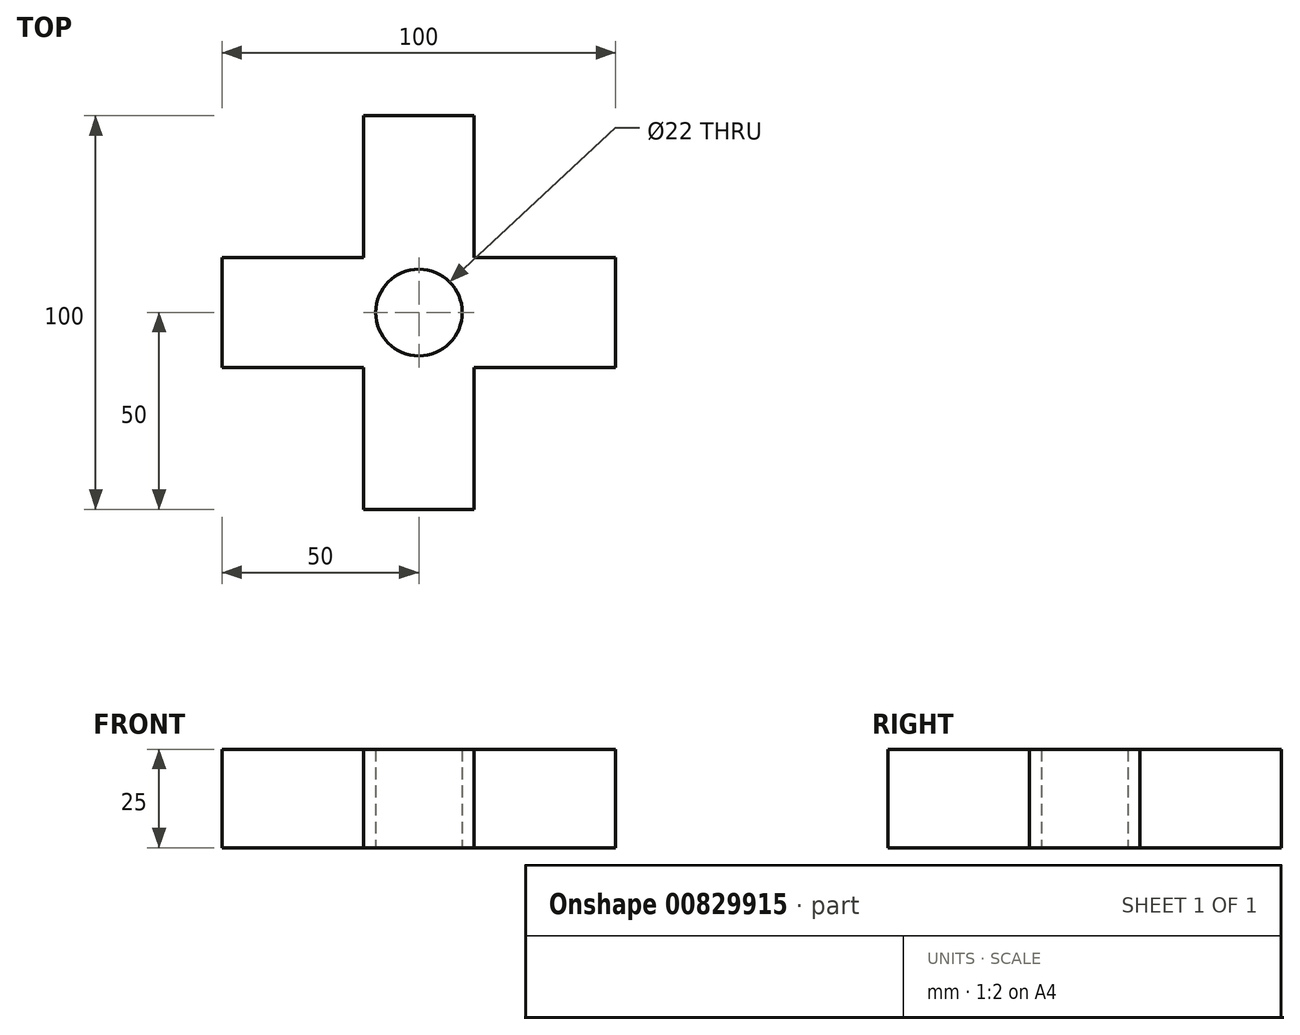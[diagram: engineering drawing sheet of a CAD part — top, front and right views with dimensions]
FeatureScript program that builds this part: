
annotation { "Feature Type Name" : "Feature", "Feature Type Description" : "" }
export const myFeature = defineFeature(function(context is Context, id is Id, definition is map)
    precondition{}
    {
        {
            var Q0;
            Q0=qCreatedBy(makeId("Top.planeOp"),FACE);
            var sketch = newSketch(context, id + "F0", { "sketchPlane" : qUnion([Q0])});
            skCircle(sketch, "E0", {"center": v(0, 0) * mm, "radius": 11 * mm});
            skPoint(sketch, "E1.oppositeSnap0", {"position": v(14, 7) * mm});
            skLineSegment(sketch, "E2.top", {"start": v(-14, 50) * mm, "end": v(14, 50) * mm});
            skLineSegment(sketch, "E2.left", {"start": v(-14, 14) * mm, "end": v(-14, 50) * mm});
            skLineSegment(sketch, "E2.right", {"start": v(14, 14) * mm, "end": v(14, 50) * mm});
            skLineSegment(sketch, "E3.bottom", {"start": v(14, 14) * mm, "end": v(50, 14) * mm});
            skLineSegment(sketch, "E3.top", {"start": v(14, -14) * mm, "end": v(50, -14) * mm});
            skLineSegment(sketch, "E3.right", {"start": v(50, 14) * mm, "end": v(50, -14) * mm});
            skLineSegment(sketch, "E4.top", {"start": v(-14, -50) * mm, "end": v(14, -50) * mm});
            skLineSegment(sketch, "E4.left", {"start": v(-14, -14) * mm, "end": v(-14, -50) * mm});
            skLineSegment(sketch, "E4.right", {"start": v(14, -14) * mm, "end": v(14, -50) * mm});
            skLineSegment(sketch, "E5.bottom", {"start": v(-14, 14) * mm, "end": v(-50, 14) * mm});
            skLineSegment(sketch, "E5.top", {"start": v(-14, -14) * mm, "end": v(-50, -14) * mm});
            skLineSegment(sketch, "E5.right", {"start": v(-50, 14) * mm, "end": v(-50, -14) * mm});
            skPoint(sketch, "E1.right.end.orphan", {"position": v(14, -14) * mm});
            skPoint(sketch, "E6.orphan", {"position": v(14, 0) * mm});
            skPoint(sketch, "E7.left.end.orphan", {"position": v(0, 14) * mm});
            skSolve(sketch);
        }
        {
            var Q0;
            Q0 = qSketchRegion(id + "F0", true);
            extrude(context, id + "F1", {"entities" : qUnion([Q0]), "depth" : 25 * mm, "offsetDistance" : 25 * mm});
        }
    });
